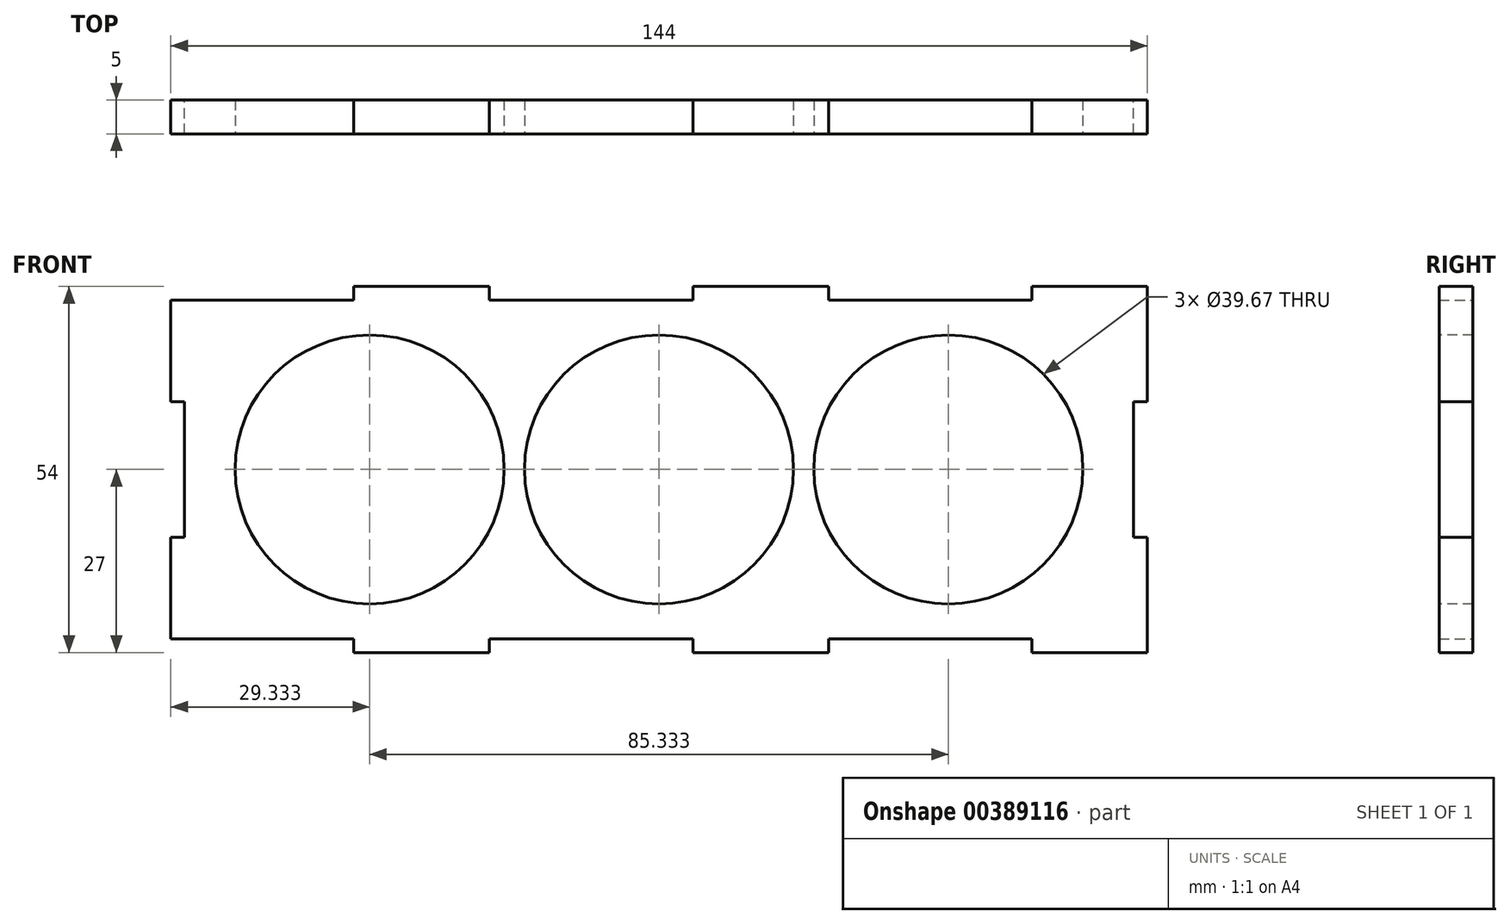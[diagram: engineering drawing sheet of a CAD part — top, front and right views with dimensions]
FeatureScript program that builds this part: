
annotation { "Feature Type Name" : "Feature", "Feature Type Description" : "" }
export const myFeature = defineFeature(function(context is Context, id is Id, definition is map)
    precondition{}
    {
        {
            var Q0;
            Q0=qCreatedBy(makeId("Front.planeOp"),FACE);
            var sketch = newSketch(context, id + "F0", { "sketchPlane" : qUnion([Q0])});
            skLineSegment(sketch, "E0", {"start": v(0, 0) * mm, "end": v(27, 0) * mm});
            skLineSegment(sketch, "E1", {"start": v(27, 0) * mm, "end": v(27, -2) * mm});
            skLineSegment(sketch, "E2", {"start": v(27, -2) * mm, "end": v(47, -2) * mm});
            skLineSegment(sketch, "E3", {"start": v(47, -2) * mm, "end": v(47, 0) * mm});
            skLineSegment(sketch, "E4", {"start": v(47, 0) * mm, "end": v(77, 0) * mm});
            skLineSegment(sketch, "E5", {"start": v(77, 0) * mm, "end": v(77, -2) * mm});
            skLineSegment(sketch, "E6", {"start": v(77, -2) * mm, "end": v(97, -2) * mm});
            skLineSegment(sketch, "E7", {"start": v(97, -2) * mm, "end": v(97, 0) * mm});
            skLineSegment(sketch, "E8", {"start": v(97, 0) * mm, "end": v(127, 0) * mm});
            skLineSegment(sketch, "E9", {"start": v(127, 0) * mm, "end": v(127, -2) * mm});
            skLineSegment(sketch, "E10", {"start": v(127, -2) * mm, "end": v(144, -2) * mm});
            skLineSegment(sketch, "E11", {"start": v(144, -2) * mm, "end": v(144, 15) * mm});
            skLineSegment(sketch, "E12", {"start": v(144, 15) * mm, "end": v(142, 15) * mm});
            skLineSegment(sketch, "E13", {"start": v(142, 15) * mm, "end": v(142, 35) * mm});
            skLineSegment(sketch, "E14", {"start": v(142, 35) * mm, "end": v(144, 35) * mm});
            skLineSegment(sketch, "E15", {"start": v(144, 35) * mm, "end": v(144, 52) * mm});
            skLineSegment(sketch, "E16", {"start": v(144, 52) * mm, "end": v(127, 52) * mm});
            skLineSegment(sketch, "E17", {"start": v(127, 52) * mm, "end": v(127, 50) * mm});
            skLineSegment(sketch, "E18", {"start": v(127, 50) * mm, "end": v(97, 50) * mm});
            skLineSegment(sketch, "E19", {"start": v(97, 50) * mm, "end": v(97, 52) * mm});
            skLineSegment(sketch, "E20", {"start": v(97, 52) * mm, "end": v(77, 52) * mm});
            skLineSegment(sketch, "E21", {"start": v(77, 52) * mm, "end": v(77, 50) * mm});
            skLineSegment(sketch, "E22", {"start": v(77, 50) * mm, "end": v(47, 50) * mm});
            skLineSegment(sketch, "E23", {"start": v(47, 50) * mm, "end": v(47, 52) * mm});
            skLineSegment(sketch, "E24", {"start": v(47, 52) * mm, "end": v(27, 52) * mm});
            skLineSegment(sketch, "E25", {"start": v(27, 52) * mm, "end": v(27, 50) * mm});
            skLineSegment(sketch, "E26", {"start": v(27, 50) * mm, "end": v(0, 50) * mm});
            skLineSegment(sketch, "E27", {"start": v(0, 50) * mm, "end": v(0, 35) * mm});
            skLineSegment(sketch, "E28", {"start": v(0, 35) * mm, "end": v(2, 35) * mm});
            skLineSegment(sketch, "E29", {"start": v(2, 35) * mm, "end": v(2, 15) * mm});
            skLineSegment(sketch, "E30", {"start": v(2, 15) * mm, "end": v(0, 15) * mm});
            skLineSegment(sketch, "E31", {"start": v(0, 15) * mm, "end": v(0, 0) * mm});
            skSolve(sketch);
        }
        {
            var Q0;
            Q0=makeQuery(id+"F0.imprint","IMPRINT",FACE,{"disambiguationData":[TD([[makeQuery(id+"F0.imprint","IMPRINT",EDGE,{"derivedFrom":sQuery(id+"F0.wireOp",EDGE,"E0")}),1.0]])]});
            extrude(context, id + "F1", {"entities" : qUnion([Q0]), "depth" : 5 * mm});
        }
        {
            var Q0;
            Q0=makeQuery(id+"F1.opExtrude","CAP_FACE",FACE,{"disambiguationData":[OSD([sQuery(id+"F0.wireOp",EDGE,"E0"),sQuery(id+"F0.wireOp",EDGE,"E1"),sQuery(id+"F0.wireOp",EDGE,"E2"),sQuery(id+"F0.wireOp",EDGE,"E3"),sQuery(id+"F0.wireOp",EDGE,"E4"),sQuery(id+"F0.wireOp",EDGE,"E5"),sQuery(id+"F0.wireOp",EDGE,"E6"),sQuery(id+"F0.wireOp",EDGE,"E7"),sQuery(id+"F0.wireOp",EDGE,"E8"),sQuery(id+"F0.wireOp",EDGE,"E9"),sQuery(id+"F0.wireOp",EDGE,"E10"),sQuery(id+"F0.wireOp",EDGE,"E11"),sQuery(id+"F0.wireOp",EDGE,"E12"),sQuery(id+"F0.wireOp",EDGE,"E13"),sQuery(id+"F0.wireOp",EDGE,"E14"),sQuery(id+"F0.wireOp",EDGE,"E15"),sQuery(id+"F0.wireOp",EDGE,"E16"),sQuery(id+"F0.wireOp",EDGE,"E17"),sQuery(id+"F0.wireOp",EDGE,"E18"),sQuery(id+"F0.wireOp",EDGE,"E19"),sQuery(id+"F0.wireOp",EDGE,"E20"),sQuery(id+"F0.wireOp",EDGE,"E21"),sQuery(id+"F0.wireOp",EDGE,"E22"),sQuery(id+"F0.wireOp",EDGE,"E23"),sQuery(id+"F0.wireOp",EDGE,"E24"),sQuery(id+"F0.wireOp",EDGE,"E25"),sQuery(id+"F0.wireOp",EDGE,"E26"),sQuery(id+"F0.wireOp",EDGE,"E27"),sQuery(id+"F0.wireOp",EDGE,"E28"),sQuery(id+"F0.wireOp",EDGE,"E29"),sQuery(id+"F0.wireOp",EDGE,"E30"),sQuery(id+"F0.wireOp",EDGE,"E31")])],"isStart":false});
            var sketch = newSketch(context, id + "F2", { "sketchPlane" : qUnion([Q0])});
            skCircle(sketch, "E32", {"center": v(114.67, 25) * mm, "radius": 19.83 * mm});
            skCircle(sketch, "E33", {"center": v(72, 25) * mm, "radius": 19.83 * mm});
            skCircle(sketch, "E34", {"center": v(29.33, 25) * mm, "radius": 19.83 * mm});
            skPoint(sketch, "E35", {"position": v(142, 25) * mm});
            skSolve(sketch);
        }
        {
            var Q0;
            Q0=makeQuery(id+"F2.imprint","IMPRINT",FACE,{"disambiguationData":[TD([[makeQuery(id+"F2.imprint","IMPRINT",EDGE,{"derivedFrom":sQuery(id+"F2.wireOp",EDGE,"E33")}),1.0]])]});
            var Q1;
            Q1=makeQuery(id+"F2.imprint","IMPRINT",FACE,{"disambiguationData":[TD([[makeQuery(id+"F2.imprint","IMPRINT",EDGE,{"derivedFrom":sQuery(id+"F2.wireOp",EDGE,"E32")}),1.0]])]});
            var Q2;
            Q2=makeQuery(id+"F2.imprint","IMPRINT",FACE,{"disambiguationData":[TD([[makeQuery(id+"F2.imprint","IMPRINT",EDGE,{"derivedFrom":sQuery(id+"F2.wireOp",EDGE,"E34")}),1.0]])]});
            extrude(context, id + "F3", {"entities" : qUnion([Q0, Q1, Q2]), "operationType" : NewBodyOperationType.REMOVE, "oppositeDirection" : true, "depth" : 25 * mm});
        }
    });
